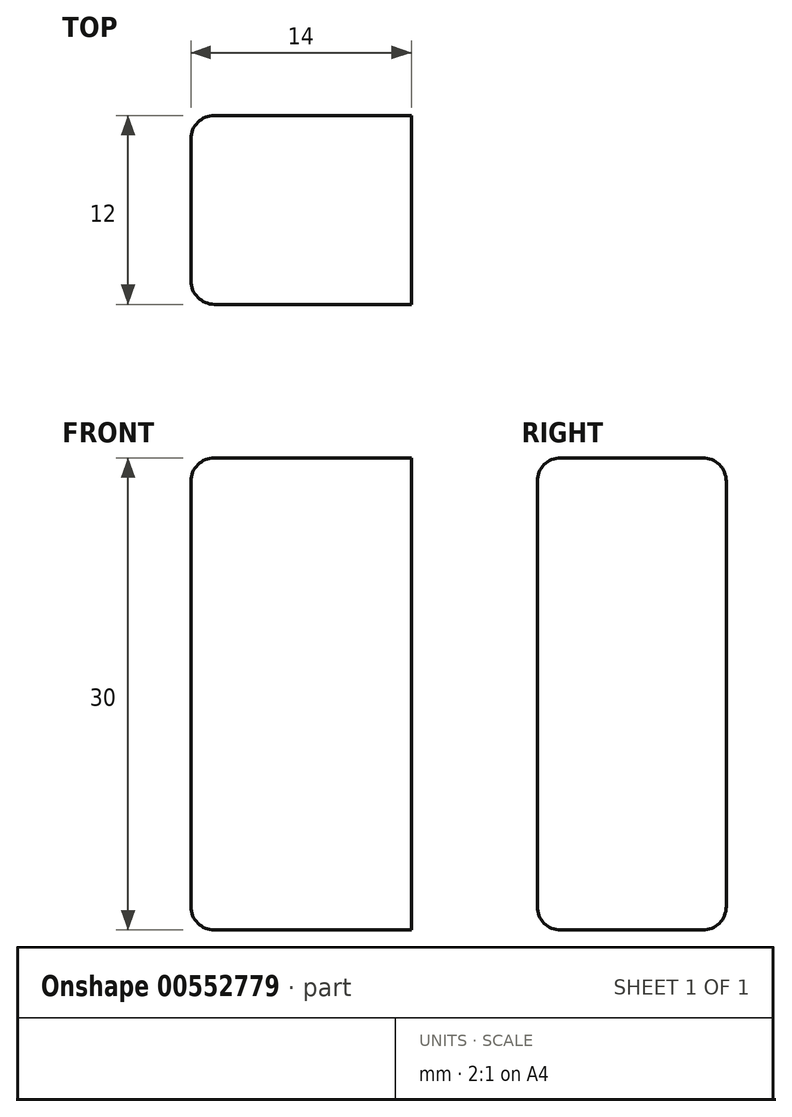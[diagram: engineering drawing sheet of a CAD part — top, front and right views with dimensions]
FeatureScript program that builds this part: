
annotation { "Feature Type Name" : "Feature", "Feature Type Description" : "" }
export const myFeature = defineFeature(function(context is Context, id is Id, definition is map)
    precondition{}
    {
        {
            var Q0;
            Q0=qCreatedBy(makeId("Front.planeOp"),FACE);
            var sketch = newSketch(context, id + "F0", { "sketchPlane" : qUnion([Q0])});
            skLineSegment(sketch, "E0.bottom", {"start": v(0, 0) * mm, "end": v(-14, 0) * mm});
            skLineSegment(sketch, "E0.top", {"start": v(0, 30) * mm, "end": v(-14, 30) * mm});
            skLineSegment(sketch, "E0.left", {"start": v(0, 0) * mm, "end": v(0, 30) * mm});
            skLineSegment(sketch, "E0.right", {"start": v(-14, 0) * mm, "end": v(-14, 30) * mm});
            skSolve(sketch);
        }
        {
            var Q0;
            Q0 = qSketchRegion(id + "F0", true);
            extrude(context, id + "F1", {"entities" : qUnion([Q0]), "depth" : 12 * mm, "offsetDistance" : 25 * mm});
        }
        {
            var Q0;
            Q0=makeQuery(id+"F1.opExtrude","SWEPT_EDGE",EDGE,{"disambiguationData":[OSD([sQuery(id+"F0.wireOp",EDGE,"E0.top"),sQuery(id+"F0.wireOp",EDGE,"E0.right")])]});
            var Q1;
            Q1=makeQuery(id+"F1.opExtrude","CAP_EDGE",EDGE,{"disambiguationData":[OSD([sQuery(id+"F0.wireOp",EDGE,"E0.top")])],"isStart":false});
            var Q2;
            Q2=makeQuery(id+"F1.opExtrude","CAP_EDGE",EDGE,{"disambiguationData":[OSD([sQuery(id+"F0.wireOp",EDGE,"E0.top")])],"isStart":true});
            var Q3;
            Q3=makeQuery(id+"F1.opExtrude","CAP_EDGE",EDGE,{"disambiguationData":[OSD([sQuery(id+"F0.wireOp",EDGE,"E0.right")])],"isStart":false});
            var Q4;
            Q4=makeQuery(id+"F1.opExtrude","CAP_EDGE",EDGE,{"disambiguationData":[OSD([sQuery(id+"F0.wireOp",EDGE,"E0.right")])],"isStart":true});
            var Q5;
            Q5=makeQuery(id+"F1.opExtrude","SWEPT_EDGE",EDGE,{"disambiguationData":[OSD([sQuery(id+"F0.wireOp",EDGE,"E0.bottom"),sQuery(id+"F0.wireOp",EDGE,"E0.right")])]});
            var Q6;
            Q6=makeQuery(id+"F1.opExtrude","CAP_EDGE",EDGE,{"disambiguationData":[OSD([sQuery(id+"F0.wireOp",EDGE,"E0.bottom")])],"isStart":false});
            var Q7;
            Q7=makeQuery(id+"F1.opExtrude","CAP_EDGE",EDGE,{"disambiguationData":[OSD([sQuery(id+"F0.wireOp",EDGE,"E0.bottom")])],"isStart":true});
            fillet(context, id + "F2", {"entities" : qUnion([Q0, Q1, Q2, Q3, Q4, Q5, Q6, Q7]), "radius" : 1.5 * mm, "tangentPropagation" : true, "allowEdgeOverflow" : false});
        }
    });
